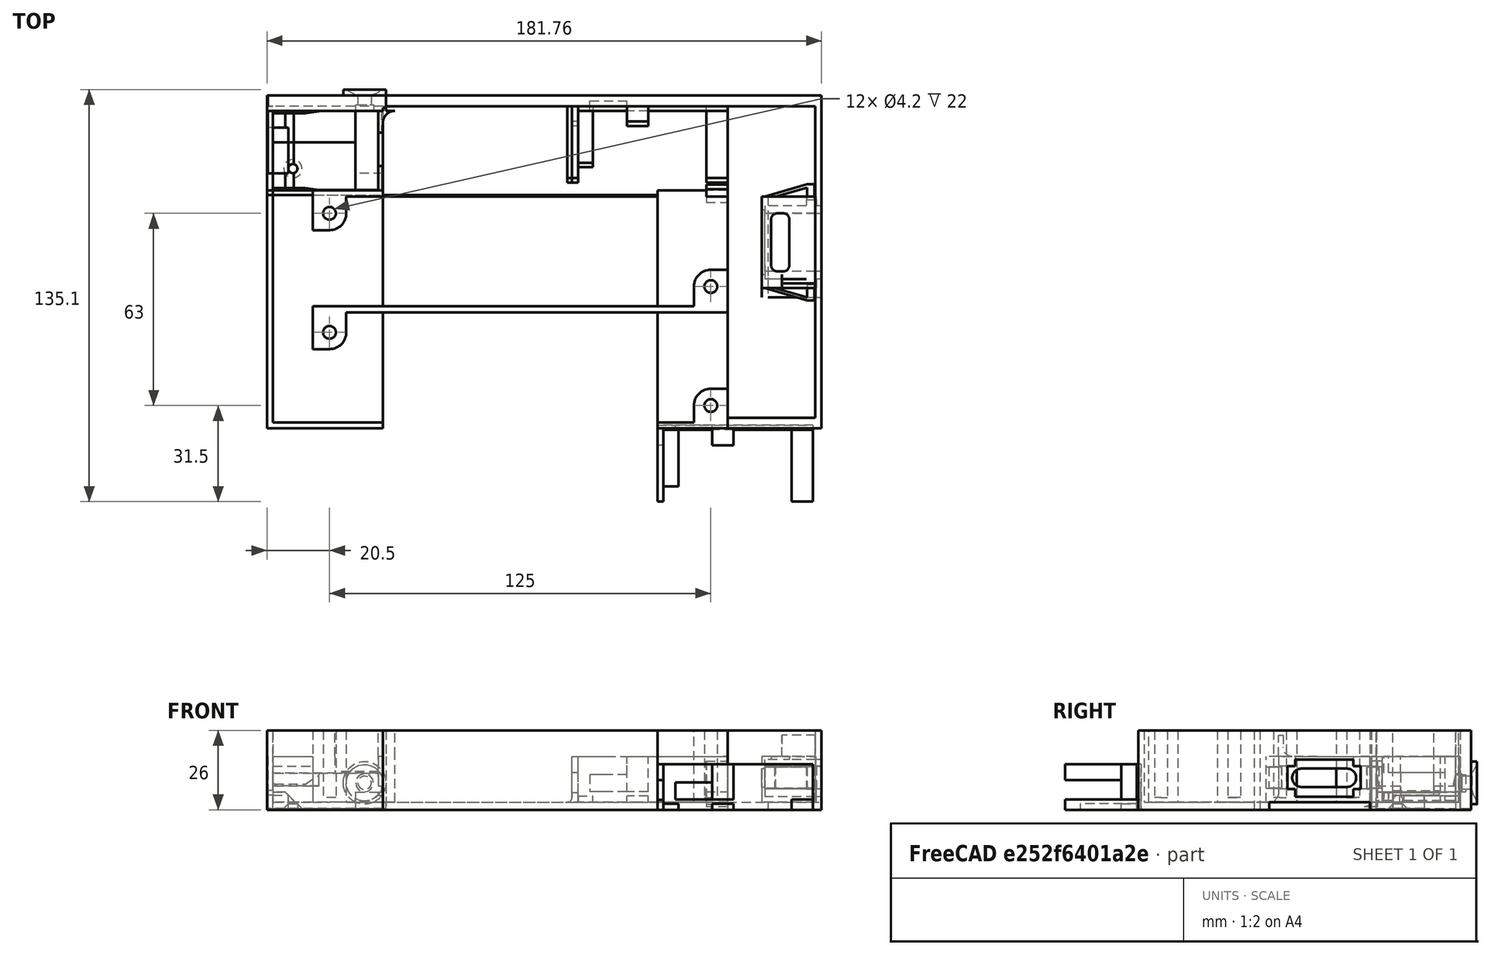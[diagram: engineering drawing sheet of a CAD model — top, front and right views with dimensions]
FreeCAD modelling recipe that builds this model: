
FCSTD DOCUMENT  (FreeCAD 0.21R33771 (Git))
Label: station.lamp.2x42V
License: All rights reserved
LicenseURL: http://en.wikipedia.org/wiki/All_rights_reserved
objects: Part::Extrusion×67, Part::Part2DObjectPython×53, Part::Feature×40, Part::FeaturePython×36, Part::MultiFuse×31, Part::Cut×25, Part::Refine×12, App::DocumentObjectGroup×10, Part::Fuse×5, Part::Box×1
note: 270 computed .brp shape members not serialized (recipe doc carries the construction recipe); baked Part::Feature solids carry a one-line shape summary decoded from their .brp

FEATURE [Part::Box] Box  label="Cube"
  AttacherType = Attacher::AttachEngine3D
  Height = 22
  Length = 11
  Width = 12
FEATURE [Part::Part2DObjectPython] Circle  # Draft 2D object (typed FeaturePython)
  Area = 13.8544
  FirstAngle = 0
  LastAngle = 0
  MakeFace = true
  Placement = pos=(5.5,6.5,22) rot=(0,0,1;0rad)
  Radius = 2.1
FEATURE [Part::Extrusion] Extrusion
  Base = -> Circle
  Dir = (0,0,-8)
  DirMode = 0
  FaceMakerClass = Part::FaceMakerBullseye
  LengthFwd = 0
  LengthRev = 0
  Solid = true
  Symmetric = false
FEATURE [Part::Cut] Cut
  Base = -> Box
  Tool = -> Extrusion
FEATURE [Part::Part2DObjectPython] Rectangle  # Draft 2D object (typed FeaturePython)
  Area = 971.593
  ChamferSize = 0
  Columns = 1
  FilletRadius = 0
  Height = 29.7354
  Length = 32.6747
  MakeFace = true
  Placement = pos=(5.5,6.5,22) rot=(0,0,1;0rad)
  Rows = 1
FEATURE [Part::Part2DObjectPython] Circle001  # Draft 2D object (typed FeaturePython)
  Area = 95.0332
  FirstAngle = 0
  LastAngle = 0
  MakeFace = true
  Placement = pos=(5.5,6.5,22) rot=(0,0,1;0rad)
  Radius = 5.5
FEATURE [Part::Extrusion] Extrusion001
  Base = -> Rectangle
  Dir = (0,0,-32.8426)
  DirMode = 0
  FaceMakerClass = Part::FaceMakerBullseye
  LengthFwd = 0
  LengthRev = 0
  Solid = true
  Symmetric = false
FEATURE [Part::Extrusion] Extrusion002
  Base = -> Circle001
  Dir = (0,0,-44.3564)
  DirMode = 0
  FaceMakerClass = Part::FaceMakerBullseye
  LengthFwd = 0
  LengthRev = 0
  Solid = true
  Symmetric = false
FEATURE [Part::Cut] Cut001
  Base = -> Extrusion001
  Tool = -> Extrusion002
FEATURE [Part::Cut] Cut002
  Base = -> Cut
  Placement = pos=(136,-37,22) rot=(0,1,0;3.14159rad)
  Tool = -> Cut001
FEATURE [Part::FeaturePython] Clone  label="Cut003"  # Draft clone (typed FeaturePython)
  AttacherType = Attacher::AttachEngine3D
  Fuse = false
  Objects = -> [Cut002]
  Placement = pos=(0,1e-15,22) rot=(1,0,0;3.14159rad)
  Scale = (1,1,1)
FEATURE [Part::Part2DObjectPython] Circle002  # Draft 2D object (typed FeaturePython)
  Area = 13.8544
  FirstAngle = 0
  LastAngle = 0
  MakeFace = true
  Placement = pos=(5.5,-6.5,0) rot=(1,0,0;3.14159rad)
  Radius = 2.1
FEATURE [Part::Part2DObjectPython] Circle003  # Draft 2D object (typed FeaturePython)
  Area = 13.8544
  FirstAngle = 0
  LastAngle = 0
  MakeFace = true
  Placement = pos=(130.5,-30.5,3e-15) rot=(1,0,0;3.14159rad)
  Radius = 2.1
FEATURE [Part::Extrusion] Extrusion003
  Base = -> Circle003
  Dir = (0,0,62.0391)
  DirMode = 0
  FaceMakerClass = Part::FaceMakerBullseye
  LengthFwd = 0
  LengthRev = 0
  Solid = true
  Symmetric = false
FEATURE [Part::Extrusion] Extrusion004
  Base = -> Circle002
  Dir = (0,0,161.733)
  DirMode = 0
  FaceMakerClass = Part::FaceMakerBullseye
  LengthFwd = 0
  LengthRev = 0
  Solid = true
  Symmetric = false
FEATURE [Part::Cut] Cut003  label="Cut004"
  Base = -> Cut002
  Tool = -> Extrusion003
FEATURE [Part::Cut] Cut004  label="Cut005"
  Base = -> Clone
  Tool = -> Extrusion004
FEATURE [Part::Part2DObjectPython] Rectangle001  # Draft 2D object (typed FeaturePython)
  Area = 851
  ChamferSize = 0
  Columns = 1
  FilletRadius = 0
  Height = 37
  Length = 23
  MakeFace = true
  Placement = pos=(136,-37,4e-15) rot=(0,1,0;3.14159rad)
  Rows = 1
FEATURE [Part::Part2DObjectPython] Clone2D  label="Rectangle001 (2D)"  # Draft 2D object (typed FeaturePython)
  Fuse = false
  Objects = -> [Rectangle001]
  Placement = pos=(23,-37,4e-15) rot=(0,1,0;3.14159rad)
  Scale = (1,1,1)
FEATURE [Part::Extrusion] Extrusion005
  Base = -> Clone2D
  Dir = (0,0,-4)
  DirMode = 0
  FaceMakerClass = Part::FaceMakerBullseye
  LengthFwd = 0
  LengthRev = 0
  Solid = true
  Symmetric = false
FEATURE [Part::Extrusion] Extrusion006
  Base = -> Rectangle001
  Dir = (0,0,-4)
  DirMode = 0
  FaceMakerClass = Part::FaceMakerBullseye
  LengthFwd = 0
  LengthRev = 0
  Solid = true
  Symmetric = false
FEATURE [Part::Feature] Face
  Placement = pos=(0,1e-15,22) rot=(1,0,0;3.14159rad)
  shape: bbox 11 x 2e-07 x 22 mm, 1 faces, 0 solids (baked)
FEATURE [Part::Extrusion] Extrusion007
  Base = -> Face
  Dir = (0,1,-1e-16)
  DirMode = 0
  FaceMakerClass = Part::FaceMakerBullseye
  LengthFwd = 0
  LengthRev = 0
  Solid = true
  Symmetric = false
FEATURE [Part::Feature] Face001
  shape: bbox 23 x 2e-07 x 4 mm, 1 faces, 0 solids (baked)
FEATURE [Part::Extrusion] Extrusion008
  Base = -> Face001
  Dir = (-6e-16,1,0)
  DirMode = 0
  FaceMakerClass = Part::FaceMakerBullseye
  LengthFwd = 0
  LengthRev = 0
  Solid = true
  Symmetric = false
FEATURE [Part::Feature] Face002
  shape: bbox 23 x 2e-07 x 4 mm, 1 faces, 0 solids (baked)
FEATURE [Part::Extrusion] Extrusion009
  Base = -> Face002
  Dir = (-6e-16,1,0)
  DirMode = 0
  FaceMakerClass = Part::FaceMakerBullseye
  LengthFwd = 0
  LengthRev = 0
  Solid = true
  Symmetric = false
FEATURE [Part::Part2DObjectPython] Rectangle002  # Draft 2D object (typed FeaturePython)
  Area = 3536
  ChamferSize = 0
  Columns = 1
  FilletRadius = 0
  Height = 26
  Length = 136
  MakeFace = true
  Placement = pos=(136,1,-4) rot=(0,0.707107,0.707107;3.14159rad)
  Rows = 1
FEATURE [Part::Extrusion] Extrusion010
  Base = -> Rectangle002
  Dir = (0,2,-4e-16)
  DirMode = 0
  FaceMakerClass = Part::FaceMakerBullseye
  LengthFwd = 0
  LengthRev = 0
  Solid = true
  Symmetric = false
FEATURE [Part::MultiFuse] Fusion
  Placement = pos=(-1.4e-14,40,0) rot=(0,0,1;0rad)
  Shapes = -> [Extrusion005,Cut004,Cut003,Extrusion006]
FEATURE [Part::FeaturePython] Clone001  label="Fusion001"  # Draft clone (typed FeaturePython)
  AttacherType = Attacher::AttachEngine3D
  Fuse = false
  Objects = -> [Fusion]
  Scale = (1,1,1)
FEATURE [Part::MultiFuse] Fusion001  label="Fusion002"
  Shapes = -> [Extrusion007,Extrusion008,Extrusion010,Clone001,Fusion]
FEATURE [Part::MultiFuse] Fusion002  label="Fusion003"
  Shapes = -> [Extrusion009,Fusion001]
FEATURE [Part::Refine] Fusion003  label="Fusion004"
  Source = -> Fusion002
FEATURE [Part::Refine] Slice001_child008  label="Slice001.008"
  Placement = pos=(63.9271,122.311,196.55) rot=(0,0,1;0rad)
FEATURE [Part::Part2DObjectPython] Rectangle003  # Draft 2D object (typed FeaturePython)
  Area = 3532.71
  ChamferSize = 0
  Columns = 1
  FilletRadius = 0
  Height = 62.6067
  Length = 56.4271
  MakeFace = true
  Placement = pos=(151.02,67.5086,-24.944) rot=(1,0,0;1.5708rad)
  Rows = 1
FEATURE [Part::FeaturePython] Slice  # WARN: FeaturePython — macro-defined, semantics opaque (R4)
  Base = -> Slice001_child008
  Mode = 1
  Tolerance = 0
  Tools = -> [Rectangle003]
FEATURE [Part::FeaturePython] Slice_child1  label="Slice.1"  # WARN: FeaturePython — macro-defined, semantics opaque (R4)
  Base = -> Slice
  FilterType = 1
  Invert = false
  OverrideMaxVal = 0
  WindowFrom = 80
  WindowTo = 100
  items = 1
FEATURE [Part::FeaturePython] Slice_child2  label="Slice.2"  # WARN: FeaturePython — macro-defined, semantics opaque (R4)
  Base = -> Slice
  FilterType = 1
  Invert = false
  OverrideMaxVal = 0
  WindowFrom = 80
  WindowTo = 100
  items = 2
FEATURE [Part::Part2DObjectPython] Rectangle004  # Draft 2D object (typed FeaturePython)
  Area = 16535.2
  ChamferSize = 0
  Columns = 1
  FilletRadius = 0
  Height = 229.122
  Length = 72.1676
  MakeFace = true
  Placement = pos=(178.703,-37,-145.137) rot=(0,0.707107,0.707107;3.14159rad)
  Rows = 1
FEATURE [Part::Feature] Face003
  shape: bbox 9.495e-05 x 4.3 x 15 mm, 1 faces, 0 solids (baked)
FEATURE [Part::Extrusion] Extrusion011
  Base = -> Face003
  Dir = (4.5,4.14e-14,-2.35167e-10)
  DirMode = 0
  FaceMakerClass = Part::FaceMakerBullseye
  LengthFwd = 0
  LengthRev = 0
  Placement = pos=(-0.7,1,0) rot=(0,0,1;0rad)
  Solid = true
  Symmetric = false
FEATURE [Part::Part2DObjectPython] Rectangle005  # Draft 2D object (typed FeaturePython)
  Area = 2512.66
  ChamferSize = 0
  Columns = 1
  FilletRadius = 0
  Height = 57.2002
  Length = 43.9275
  MakeFace = true
  Placement = pos=(113.7,-22.7052,-12.794) rot=(0.57735,-0.57735,-0.57735;2.0944rad)
  Rows = 1
FEATURE [Part::Part2DObjectPython] Rectangle006  # Draft 2D object (typed FeaturePython)
  Area = 65540.4
  ChamferSize = 0
  Columns = 1
  FilletRadius = 0
  Height = 220.903
  Length = 296.693
  MakeFace = true
  Placement = pos=(-69.999,-3.62e-14,-154.145) rot=(1,0,0;1.5708rad)
  Rows = 1
FEATURE [Part::FeaturePython] Slice003  # WARN: FeaturePython — macro-defined, semantics opaque (R4)
  Base = -> Fusion003
  Mode = 1
  Tolerance = 0
  Tools = -> [Rectangle006]
FEATURE [App::DocumentObjectGroup] GrExplode_Slice003  label="Exploded Slice003"
FEATURE [Part::FeaturePython] Slice003_child0  label="Slice003.0"  # WARN: FeaturePython — macro-defined, semantics opaque (R4)
  Base = -> Slice003
  FilterType = 1
  Invert = false
  OverrideMaxVal = 0
  WindowFrom = 80
  WindowTo = 100
  items = 0
FEATURE [Part::FeaturePython] Slice003_child1  label="Slice003.1"  # WARN: FeaturePython — macro-defined, semantics opaque (R4)
  Base = -> Slice003
  FilterType = 1
  Invert = false
  OverrideMaxVal = 0
  Placement = pos=(0,1,0) rot=(0,0,1;0rad)
  WindowFrom = 80
  WindowTo = 100
  items = 1
FEATURE [Part::FeaturePython] Slice003_child2  label="Slice003.2"  # WARN: FeaturePython — macro-defined, semantics opaque (R4)
  Base = -> Slice003
  FilterType = 1
  Invert = false
  OverrideMaxVal = 0
  Placement = pos=(0,1,0) rot=(0,0,1;0rad)
  WindowFrom = 80
  WindowTo = 100
  items = 2
FEATURE [Part::Part2DObjectPython] Line009  # Draft 2D object (typed FeaturePython)
  Area = 0
  ChamferSize = 0
  Closed = false
  End = (23,-17.5,-1.5)
  FilletRadius = 0
  Length = 1.5
  MakeFace = true
  Placement = pos=(23,-17.5,4e-15) rot=(0.57735,0.57735,0.57735;2.0944rad)
  Points = (2) [(0,0,0),(0,-1.5,-2.66454e-15)]
  Start = (23,-17.5,3.6e-15)
  Subdivisions = 0
FEATURE [Part::Feature] Face004
  shape: bbox 23 x 37 x 9.495e-05 mm, 1 faces, 0 solids (baked)
FEATURE [Part::Extrusion] Extrusion012
  Base = -> Face004
  Dir = (0,0,-1.5)
  DirMode = 0
  FaceMakerClass = Part::FaceMakerBullseye
  LengthFwd = 0
  LengthRev = 0
  Solid = true
  Symmetric = false
FEATURE [Part::Feature] Face005
  Placement = pos=(-1.4e-14,40,0) rot=(0,0,1;0rad)
  shape: bbox 23 x 37 x 9.495e-05 mm, 1 faces, 0 solids (baked)
FEATURE [Part::Extrusion] Extrusion013
  Base = -> Face005
  Dir = (0,0,-1.5)
  DirMode = 0
  FaceMakerClass = Part::FaceMakerBullseye
  LengthFwd = 0
  LengthRev = 0
  Solid = true
  Symmetric = false
FEATURE [Part::Feature] Face006
  Placement = pos=(-1.4e-14,40,0) rot=(0,0,1;0rad)
  shape: bbox 23 x 37 x 9.495e-05 mm, 1 faces, 0 solids (baked)
FEATURE [Part::Extrusion] Extrusion014
  Base = -> Face006
  Dir = (0,0,-1.5)
  DirMode = 0
  FaceMakerClass = Part::FaceMakerBullseye
  LengthFwd = 0
  LengthRev = 0
  Solid = true
  Symmetric = false
FEATURE [Part::Feature] Face007
  shape: bbox 23 x 37 x 2.037e-05 mm, 1 faces, 0 solids (baked)
FEATURE [Part::Extrusion] Extrusion015
  Base = -> Face007
  Dir = (0,0,-1.5)
  DirMode = 0
  FaceMakerClass = Part::FaceMakerBullseye
  LengthFwd = 0
  LengthRev = 0
  Solid = true
  Symmetric = false
FEATURE [Part::Part2DObjectPython] Rectangle007  # Draft 2D object (typed FeaturePython)
  Area = 5888.28
  ChamferSize = 0
  Columns = 1
  FilletRadius = 0
  Height = 60.4657
  Length = 97.3822
  MakeFace = true
  Placement = pos=(94.0945,-36,-42.8831) rot=(1,0,0;1.5708rad)
  Rows = 1
FEATURE [Part::FeaturePython] Slice_child0  label="Slice.0"  # WARN: FeaturePython — macro-defined, semantics opaque (R4)
  Base = -> Slice
  FilterType = 1
  Invert = false
  OverrideMaxVal = 0
  Placement = pos=(81.7528,194.877,-8.54915) rot=(0,0,-1;1.5708rad)
  WindowFrom = 80
  WindowTo = 100
  items = 0
FEATURE [Part::MultiFuse] Fusion004  label="Fusion005"
  Placement = pos=(93.9914,120.377,-12.5492) rot=(0,0,-1;1.5708rad)
  Shapes = -> [Slice_child1,Slice_child2]
FEATURE [App::DocumentObjectGroup] GrExplode_Slice  label="Exploded Slice"
  Group = -> [Fusion004]
FEATURE [Part::FeaturePython] Slice001  # WARN: FeaturePython — macro-defined, semantics opaque (R4)
  Base = -> Fusion004
  Mode = 1
  Tolerance = 0
  Tools = -> [Rectangle004]
FEATURE [Part::FeaturePython] Slice001_child1  label="Slice001.1"  # WARN: FeaturePython — macro-defined, semantics opaque (R4)
  Base = -> Slice001
  FilterType = 1
  Invert = false
  OverrideMaxVal = 0
  Placement = pos=(3.2,1,1.5) rot=(0,0,1;0rad)
  WindowFrom = 80
  WindowTo = 100
  items = 1
FEATURE [Part::FeaturePython] Slice001_child2  label="Slice001.2"  # WARN: FeaturePython — macro-defined, semantics opaque (R4)
  Base = -> Slice001
  FilterType = 1
  Invert = false
  OverrideMaxVal = 0
  Placement = pos=(-0.7,1,0) rot=(0,0,1;0rad)
  WindowFrom = 80
  WindowTo = 100
  items = 2
FEATURE [Part::FeaturePython] Slice002  # WARN: FeaturePython — macro-defined, semantics opaque (R4)
  Base = -> Slice001_child1
  Mode = 1
  Tolerance = 0
  Tools = -> [Rectangle005]
FEATURE [Part::FeaturePython] Slice002_child0  label="Slice002.0"  # WARN: FeaturePython — macro-defined, semantics opaque (R4)
  Base = -> Slice002
  FilterType = 1
  Invert = false
  OverrideMaxVal = 0
  Placement = pos=(-0.7,0,0) rot=(0,0,1;0rad)
  WindowFrom = 80
  WindowTo = 100
  items = 0
FEATURE [App::DocumentObjectGroup] GrExplode_Slice002  label="Exploded Slice002"
  Group = -> [Slice002_child0]
FEATURE [Part::MultiFuse] Fusion005  label="Fusion006"
  Shapes = -> [Slice003_child1,Slice003_child0,Slice003_child2,Slice001_child1,Slice001_child2,Extrusion011]
FEATURE [App::DocumentObjectGroup] GrExplode_Slice001  label="Exploded Slice001"
  Group = -> [Fusion005]
FEATURE [Part::Refine] Fusion006  label="Fusion007"
  Source = -> Fusion005
FEATURE [Part::Cut] Cut005  label="Cut006"
  Base = -> Fusion006
  Tool = -> Extrusion015
FEATURE [Part::Cut] Cut006  label="Cut007"
  Base = -> Cut005
  Tool = -> Extrusion014
FEATURE [Part::Cut] Cut007  label="Cut008"
  Base = -> Cut006
  Tool = -> Extrusion013
FEATURE [Part::Cut] Cut008  label="Cut009"
  Base = -> Cut007
  Tool = -> Extrusion012
FEATURE [Part::FeaturePython] Slice004  # WARN: FeaturePython — macro-defined, semantics opaque (R4)
  Base = -> Cut008
  Mode = 1
  Tolerance = 0
  Tools = -> [Rectangle007]
FEATURE [Part::FeaturePython] Slice004_child0  label="Slice004.0"  # WARN: FeaturePython — macro-defined, semantics opaque (R4)
  Base = -> Slice004
  FilterType = 1
  Invert = false
  OverrideMaxVal = 0
  WindowFrom = 80
  WindowTo = 100
  items = 0
FEATURE [Part::FeaturePython] Slice004_child1  label="Slice004.1"  # WARN: FeaturePython — macro-defined, semantics opaque (R4)
  Base = -> Slice004
  FilterType = 1
  Invert = false
  OverrideMaxVal = 0
  WindowFrom = 80
  WindowTo = 100
  items = 1
FEATURE [Part::FeaturePython] Slice004_child2  label="Slice004.2"  # WARN: FeaturePython — macro-defined, semantics opaque (R4)
  Base = -> Slice004
  FilterType = 1
  Invert = false
  OverrideMaxVal = 0
  WindowFrom = 80
  WindowTo = 100
  items = 2
FEATURE [Part::Part2DObjectPython] Line010  # Draft 2D object (typed FeaturePython)
  Area = 0
  ChamferSize = 0
  Closed = false
  End = (11,39,11)
  FilletRadius = 0
  Length = 1
  MakeFace = true
  Placement = pos=(11,40,11) rot=(0.57735,0.57735,0.57735;2.0944rad)
  Points = (2) [(0,0,0),(-1,0,0)]
  Start = (11,40,11)
  Subdivisions = 0
FEATURE [Part::Part2DObjectPython] Rectangle008  # Draft 2D object (typed FeaturePython)
  Area = 23.5
  ChamferSize = 0
  Columns = 1
  FilletRadius = 0
  Height = 23.5
  Length = 1
  MakeFace = true
  Placement = pos=(11,39,-1.5) rot=(0.57735,0.57735,0.57735;2.0944rad)
  Rows = 1
FEATURE [Part::Extrusion] Extrusion016
  Base = -> Rectangle008
  Dir = (12,0,0)
  DirMode = 0
  FaceMakerClass = Part::FaceMakerBullseye
  LengthFwd = 0
  LengthRev = 0
  Solid = true
  Symmetric = false
FEATURE [Part::MultiFuse] Fusion007  label="Fusion008"
  Placement = pos=(-28.7,104.6,2.5) rot=(0,0,1;0rad)
  Shapes = -> [Slice004_child1,Slice004_child2]
FEATURE [Part::Part2DObjectPython] Line012  # Draft 2D object (typed FeaturePython)
  Area = 0
  ChamferSize = 0
  Closed = false
  End = (125,-35,11)
  FilletRadius = 0
  Length = 1
  MakeFace = true
  Placement = pos=(125,-36,11) rot=(0.57735,-0.57735,-0.57735;2.0944rad)
  Points = (2) [(0,0,0),(-1,0,0)]
  Start = (125,-36,11)
  Subdivisions = 0
FEATURE [Part::Part2DObjectPython] Rectangle009  # Draft 2D object (typed FeaturePython)
  Area = 23.5
  ChamferSize = 0
  Columns = 1
  FilletRadius = 0
  Height = 23.5
  Length = 1
  MakeFace = true
  Placement = pos=(125,-35,-1.5) rot=(0.57735,-0.57735,-0.57735;2.0944rad)
  Rows = 1
FEATURE [Part::Extrusion] Extrusion017
  Base = -> Rectangle009
  Dir = (-12,0,0)
  DirMode = 0
  FaceMakerClass = Part::FaceMakerBullseye
  LengthFwd = 0
  LengthRev = 0
  Solid = true
  Symmetric = false
FEATURE [Part::Feature] Face008
  Placement = pos=(113,-35,-1.5) rot=(0.57735,-0.57735,-0.57735;2.0944rad)
  shape: bbox 9.505e-05 x 1 x 23.5 mm, 1 faces, 0 solids (baked)
FEATURE [Part::Part2DObjectPython] Rectangle010  # Draft 2D object (typed FeaturePython)
  Area = 540.5
  ChamferSize = 0
  Columns = 1
  FilletRadius = 0
  Height = 23.5
  Length = 23
  MakeFace = true
  Placement = pos=(1.4e-14,-36,-1.5) rot=(1,0,0;1.5708rad)
  Rows = 1
FEATURE [Part::Extrusion] Extrusion019
  Base = -> Rectangle010
  Dir = (-6e-16,1,-2e-16)
  DirMode = 0
  FaceMakerClass = Part::FaceMakerBullseye
  LengthFwd = 0
  LengthRev = 0
  Solid = true
  Symmetric = false
FEATURE [Part::Feature] Face009
  Placement = pos=(23,39,-1.5) rot=(0.57735,0.57735,0.57735;2.0944rad)
  shape: bbox 9.505e-05 x 1 x 23.5 mm, 1 faces, 0 solids (baked)
FEATURE [Part::Part2DObjectPython] Rectangle011  # Draft 2D object (typed FeaturePython)
  Area = 540.5
  ChamferSize = 0
  Columns = 1
  FilletRadius = 0
  Height = 23.5
  Length = 23
  MakeFace = true
  Placement = pos=(136,40,-1.5) rot=(0,0.707107,0.707107;3.14159rad)
  Rows = 1
FEATURE [Part::Extrusion] Extrusion021
  Base = -> Rectangle011
  Dir = (0,-1,2e-16)
  DirMode = 0
  FaceMakerClass = Part::FaceMakerBullseye
  LengthFwd = 0
  LengthRev = 0
  Solid = true
  Symmetric = false
FEATURE [Part::MultiFuse] Fusion008  label="Fusion009"
  Shapes = -> [Extrusion017,Extrusion019,Extrusion016,Extrusion021,Slice004_child0]
FEATURE [Part::Refine] Fusion009  label="Fusion010"
  Source = -> Fusion008
FEATURE [Part::Part2DObjectPython] Line014  # Draft 2D object (typed FeaturePython)
  Area = 0
  ChamferSize = 0
  Closed = false
  End = (1.47e-14,-37,22)
  FilletRadius = 0
  Length = 1
  MakeFace = true
  Placement = pos=(1.4e-14,-36,22) rot=(0.57735,-0.57735,-0.57735;2.0944rad)
  Points = (2) [(0,0,0),(1,0,-1.69085e-16)]
  Start = (1.42e-14,-36,22)
  Subdivisions = 0
FEATURE [Part::Feature] Face010
  shape: bbox 23 x 9.505e-05 x 26 mm, 1 faces, 0 solids (baked)
FEATURE [Part::Extrusion] Extrusion022
  Base = -> Face010
  Dir = (6e-16,-1,2e-15)
  DirMode = 0
  FaceMakerClass = Part::FaceMakerBullseye
  LengthFwd = 0
  LengthRev = 0
  Solid = true
  Symmetric = false
FEATURE [Part::Feature] Face011
  shape: bbox 23 x 9.505e-05 x 26 mm, 1 faces, 0 solids (baked)
FEATURE [Part::Extrusion] Extrusion023
  Base = -> Face011
  Dir = (2e-16,-1,5e-16)
  DirMode = 0
  FaceMakerClass = Part::FaceMakerBullseye
  LengthFwd = 0
  LengthRev = 0
  Solid = true
  Symmetric = false
FEATURE [Part::Part2DObjectPython] Line015  # Draft 2D object (typed FeaturePython)
  Area = 0
  ChamferSize = 0
  Closed = false
  End = (23,41,22)
  FilletRadius = 0
  Length = 1
  MakeFace = true
  Placement = pos=(23,40,22) rot=(0,0,1;1.5708rad)
  Points = (2) [(0,0,0),(1,0,0)]
  Start = (23,40,22)
  Subdivisions = 0
FEATURE [Part::Feature] Face012
  shape: bbox 23 x 9.495e-05 x 26 mm, 1 faces, 0 solids (baked)
FEATURE [Part::Extrusion] Extrusion024
  Base = -> Face012
  Dir = (-2e-16,1,2e-16)
  DirMode = 0
  FaceMakerClass = Part::FaceMakerBullseye
  LengthFwd = 0
  LengthRev = 0
  Solid = true
  Symmetric = false
FEATURE [Part::Feature] Face013
  shape: bbox 23 x 9.505e-05 x 26 mm, 1 faces, 0 solids (baked)
FEATURE [Part::Extrusion] Extrusion025
  Base = -> Face013
  Dir = (-2e-16,1,1.6e-15)
  DirMode = 0
  FaceMakerClass = Part::FaceMakerBullseye
  LengthFwd = 0
  LengthRev = 0
  Solid = true
  Symmetric = false
FEATURE [Part::MultiFuse] Fusion010  label="Fusion011"
  Shapes = -> [Extrusion023,Extrusion022,Extrusion024,Extrusion025,Fusion009]
FEATURE [Part::Refine] Fusion011  label="Fusion012"
  Source = -> Fusion010
FEATURE [Part::MultiFuse] Fusion005002002014004003003002009002010004002003006003008008004007002004008002005011019002002002012002
FEATURE [Part::Part2DObjectPython] Rectangle012  # Draft 2D object (typed FeaturePython)
  ChamferSize = 0
  Columns = 1
  FilletRadius = 0
  Height = 74.0625
  Length = 50.4262
  MakeFace = true
  Placement = pos=(152.909,-168.503,-194.387) rot=(1,0,0;1.5708rad)
  Rows = 1
FEATURE [Part::Part2DObjectPython] Rectangle013  # Draft 2D object (typed FeaturePython)
  Area = 24058.8
  ChamferSize = 0
  Columns = 1
  FilletRadius = 0
  Height = 153.205
  Length = 157.037
  MakeFace = true
  Placement = pos=(77.9842,-28.2917,-189.501) rot=(0,0,-1;1.5708rad)
  Rows = 1
FEATURE [Part::FeaturePython] Slice005  # WARN: FeaturePython — macro-defined, semantics opaque (R4)
  Base = -> Fusion005002002014004003003002009002010004002003006003008008004007002004008002005011019002002002012002
  Mode = 1
  Tolerance = 0
  Tools = -> [Rectangle012]
FEATURE [Part::FeaturePython] Slice_child003  label="Slice.003"  # WARN: FeaturePython — macro-defined, semantics opaque (R4)
  Base = -> Slice005
  FilterType = 1
  Invert = false
  OverrideMaxVal = 0
  WindowFrom = 80
  WindowTo = 100
  items = 0
FEATURE [Part::FeaturePython] Slice006  # WARN: FeaturePython — macro-defined, semantics opaque (R4)
  Base = -> Slice_child003
  Mode = 1
  Tolerance = 0
  Tools = -> [Rectangle013]
FEATURE [Part::FeaturePython] Slice001_child009  label="Slice001.009"  # WARN: FeaturePython — macro-defined, semantics opaque (R4)
  Base = -> Slice006
  FilterType = 1
  Invert = false
  OverrideMaxVal = 0
  Placement = pos=(-34.5709,-121.99,188.001) rot=(0,0,1;0rad)
  WindowFrom = 80
  WindowTo = 100
  items = 1
FEATURE [Part::Refine] Slice001_child010  label="Slice001.010"
  Placement = pos=(127.549,-38.5,-261.892) rot=(0,-0.707107,0.707107;3.14159rad)
  Source = -> Slice001_child009
FEATURE [Part::Part2DObjectPython] Line019  # Draft 2D object (typed FeaturePython)
  Area = 0
  ChamferSize = 0
  Closed = false
  End = (23,-37,-1)
  FilletRadius = 0
  Length = 3
  MakeFace = true
  Placement = pos=(23,-40,-1) rot=(0.57735,0.57735,0.57735;2.0944rad)
  Points = (2) [(0,0,0),(3,2.49441e-09,-1.58593e-11)]
  Start = (23,-40,-1)
  Subdivisions = 0
FEATURE [Part::Part2DObjectPython] Rectangle014  # Draft 2D object (typed FeaturePython)
  Area = 12480.5
  ChamferSize = 0
  Columns = 1
  FilletRadius = 0
  Height = 104.133
  Length = 119.851
  MakeFace = true
  Placement = pos=(65.3633,29.745,-4) rot=(0.707107,-0.707107,0;3.14159rad)
  Rows = 1
FEATURE [Part::FeaturePython] Slice007  # WARN: FeaturePython — macro-defined, semantics opaque (R4)
  Base = -> Slice001_child010
  Mode = 1
  Tolerance = 0
  Tools = -> [Rectangle014]
FEATURE [App::DocumentObjectGroup] GrExplode_Slice007  label="Exploded Slice007"
FEATURE [Part::FeaturePython] Slice007_child0  label="Slice007.0"  # WARN: FeaturePython — macro-defined, semantics opaque (R4)
  Base = -> Slice007
  FilterType = 1
  Invert = false
  OverrideMaxVal = 0
  WindowFrom = 80
  WindowTo = 100
  items = 0
FEATURE [Part::Feature] Face014
  shape: bbox 0.0001337 x 5 x 1.65 mm, 1 faces, 0 solids (baked)
FEATURE [Part::Extrusion] Extrusion026
  Base = -> Face014
  Dir = (14.1794,4.79232e-08,2.885e-13)
  DirMode = 0
  FaceMakerClass = Part::FaceMakerBullseye
  LengthFwd = 0
  LengthRev = 0
  Solid = true
  Symmetric = false
FEATURE [Part::MultiFuse] Fusion005002002014004003003002009002010004002003006003008008004007002004008002005011019002002002012003
  Placement = pos=(-1.12479e-11,6.4929e-09,-1.6) rot=(0,0,1;0rad)
  Shapes = -> [Slice007_child0,Extrusion026]
FEATURE [Part::Part2DObjectPython] Rectangle015  # Draft 2D object (typed FeaturePython)
  Area = 189.759
  ChamferSize = 0
  Columns = 1
  FilletRadius = 0
  Height = 34.5
  Length = 5.50025
  MakeFace = true
  Placement = pos=(21.5,-52,-3.95) rot=(0,0,1;1.5708rad)
  Rows = 1
FEATURE [Part::Extrusion] Extrusion027
  Base = -> Rectangle015
  Dir = (2.2392e-09,1.32254e-08,7.85)
  DirMode = 0
  FaceMakerClass = Part::FaceMakerBullseye
  LengthFwd = 0
  LengthRev = 0
  Placement = pos=(4e-15,-1.24722e-10,-0.15) rot=(0,0,1;0rad)
  Solid = true
  Symmetric = false
FEATURE [Part::Cut] Cut009  label="Cut010"
  Base = -> Fusion005002002014004003003002009002010004002003006003008008004007002004008002005011019002002002012003
  Placement = pos=(-6.04654e-08,45.1,-38.5) rot=(-1,0,0;1.5708rad)
  Tool = -> Extrusion027
FEATURE [Part::Part2DObjectPython] Rectangle016  # Draft 2D object (typed FeaturePython)
  Area = 3801.6
  ChamferSize = 0
  Columns = 1
  FilletRadius = 0
  Height = 36
  Length = 105.6
  MakeFace = true
  Placement = pos=(23,68.6,-4) rot=(0.707107,-0.707107,0;3.14159rad)
  Rows = 1
FEATURE [Part::Extrusion] Extrusion028
  Base = -> Rectangle016
  Dir = (-4.02896e-11,9.80014e-11,2.5)
  DirMode = 0
  FaceMakerClass = Part::FaceMakerBullseye
  LengthFwd = 0
  LengthRev = 0
  Solid = true
  Symmetric = false
FEATURE [Part::Part2DObjectPython] Circle004  # Draft 2D object (typed FeaturePython)
  Area = 7.06956
  FirstAngle = 0
  LastAngle = 0
  MakeFace = true
  Placement = pos=(-6.48965,49.6501,-1.00025) rot=(1,0,0;3.14159rad)
  Radius = 1.5001
FEATURE [Part::Extrusion] Extrusion029
  Base = -> Circle004
  Dir = (-6.49882e-09,-1.24878e-09,-29.8695)
  DirMode = 0
  FaceMakerClass = Part::FaceMakerBullseye
  LengthFwd = 0
  LengthRev = 0
  Solid = true
  Symmetric = false
FEATURE [Part::Cut] Cut010  label="Cut011"
  Base = -> Extrusion028
  Tool = -> Extrusion029
FEATURE [Part::Part2DObjectPython] Rectangle017  # Draft 2D object (typed FeaturePython)
  Area = 2745.6
  ChamferSize = 0
  Columns = 1
  FilletRadius = 0
  Height = 26
  Length = 105.6
  MakeFace = true
  Placement = pos=(-13,68.6,-4) rot=(0.57735,-0.57735,-0.57735;2.0944rad)
  Rows = 1
FEATURE [Part::Part2DObjectPython] Rectangle018  # Draft 2D object (typed FeaturePython)
  Area = 47
  ChamferSize = 0
  Columns = 1
  FilletRadius = 0
  Height = 23.5
  Length = 2
  MakeFace = true
  Placement = pos=(1.3e-14,-35,-1.5) rot=(0.57735,-0.57735,-0.57735;2.0944rad)
  Rows = 1
FEATURE [Part::Extrusion] Extrusion030
  Base = -> Rectangle018
  Dir = (-13,-2.9e-15,1.4e-15)
  DirMode = 0
  FaceMakerClass = Part::FaceMakerBullseye
  LengthFwd = 0
  LengthRev = 0
  Solid = true
  Symmetric = false
FEATURE [Part::Part2DObjectPython] Line026  # Draft 2D object (typed FeaturePython)
  Area = 0
  ChamferSize = 0
  Closed = false
  End = (-15,-37,22)
  FilletRadius = 0
  Length = 2
  MakeFace = true
  Placement = pos=(-13,-37,22) rot=(0,0,1;0rad)
  Points = (2) [(0,0,0),(-2,0,0)]
  Start = (-13,-37,22)
  Subdivisions = 0
FEATURE [Part::Extrusion] Extrusion031
  Base = -> Rectangle017
  Dir = (-2,4e-16,-3.2232e-11)
  DirMode = 0
  FaceMakerClass = Part::FaceMakerBullseye
  LengthFwd = 0
  LengthRev = 0
  Solid = true
  Symmetric = false
FEATURE [Part::MultiFuse] Fusion005002002014004003003002009002010004002003006003008008004007002004008002005011019002002002012004
  Shapes = -> [Extrusion031,Extrusion030]
FEATURE [Part::MultiFuse] Fusion005002002014004003003002009002010004002003006003008008004007002004008002005011019002002002012005
  Shapes = -> [Fusion005002002014004003003002009002010004002003006003008008004007002004008002005011019002002002012004,Cut010]
FEATURE [Part::Part2DObjectPython] Rectangle019  # Draft 2D object (typed FeaturePython)
  Area = 69
  ChamferSize = 0
  Columns = 1
  FilletRadius = 0
  Height = 2.5
  Length = 27.6
  MakeFace = true
  Placement = pos=(23,41,-4) rot=(0.57735,0.57735,0.57735;2.0944rad)
  Rows = 1
FEATURE [Part::Extrusion] Extrusion032
  Base = -> Rectangle019
  Dir = (113,5.02e-14,1.82115e-09)
  DirMode = 0
  FaceMakerClass = Part::FaceMakerBullseye
  LengthFwd = 0
  LengthRev = 0
  Placement = pos=(2.6823e-11,-1.5,9.6466e-10) rot=(0,0,1;0rad)
  Solid = true
  Symmetric = false
FEATURE [Part::Part2DObjectPython] Line028  # Draft 2D object (typed FeaturePython)
  Area = 0
  ChamferSize = 0
  Closed = false
  End = (136,43.2,-1.5)
  FilletRadius = 0
  Length = 0.6
  MakeFace = true
  Placement = pos=(135.4,43.2,-1.5) rot=(0,0,1;3.14159rad)
  Points = (2) [(0,0,0),(-0.6,0,1.55798e-10)]
  Start = (135.4,43.2,-1.5)
  Subdivisions = 0
FEATURE [Part::Part2DObjectPython] Rectangle020  # Draft 2D object (typed FeaturePython)
  Area = 5716.63
  ChamferSize = 0
  Columns = 1
  FilletRadius = 0
  Height = 112.818
  Length = 50.6711
  MakeFace = true
  Placement = pos=(30.41,41,-71.6025) rot=(0,0.707107,0.707107;3.14159rad)
  Rows = 1
FEATURE [Part::FeaturePython] Slice008  # WARN: FeaturePython — macro-defined, semantics opaque (R4)
  Base = -> Fusion005002002014004003003002009002010004002003006003008008004007002004008002005011019002002002012005
  Mode = 1
  Tolerance = 0
  Tools = -> [Rectangle020]
FEATURE [Part::FeaturePython] Slice008_child0  label="Slice008.0"  # WARN: FeaturePython — macro-defined, semantics opaque (R4)
  Base = -> Slice008
  FilterType = 1
  Invert = false
  OverrideMaxVal = 0
  Placement = pos=(2.6819e-11,-1.5,9.64661e-10) rot=(0,0,1;0rad)
  WindowFrom = 80
  WindowTo = 100
  items = 0
FEATURE [App::DocumentObjectGroup] GrExplode_Slice008  label="Exploded Slice008"
  Group = -> [Slice008_child0]
FEATURE [Part::FeaturePython] Slice008_child1  label="Slice008.1"  # WARN: FeaturePython — macro-defined, semantics opaque (R4)
  Base = -> Slice008
  FilterType = 1
  Invert = false
  OverrideMaxVal = 0
  WindowFrom = 80
  WindowTo = 100
  items = 1
FEATURE [Part::Part2DObjectPython] Rectangle021  # Draft 2D object (typed FeaturePython)
  Area = 540.5
  ChamferSize = 0
  Columns = 1
  FilletRadius = 0
  Height = 23.5
  Length = 23
  MakeFace = true
  Placement = pos=(136,41,-1.5) rot=(0,0.707107,0.707107;3.14159rad)
  Rows = 1
FEATURE [Part::Extrusion] Extrusion033
  Base = -> Rectangle021
  Dir = (0,-12.9512,-2.3e-14)
  DirMode = 0
  FaceMakerClass = Part::FaceMakerBullseye
  LengthFwd = 0
  LengthRev = 0
  Solid = true
  Symmetric = false
FEATURE [Part::Cut] Cut011  label="Cut012"
  Base = -> Fusion011
  Tool = -> Extrusion033
FEATURE [Part::Feature] Face016
  Placement = pos=(-24.9,105.6,2.5) rot=(0,0,1;0rad)
  shape: bbox 9.496e-05 x 4.3 x 15 mm, 1 faces, 0 solids (baked)
FEATURE [Part::Extrusion] Extrusion034
  Base = -> Face016
  Dir = (-0.6,-5.5e-15,3.13556e-11)
  DirMode = 0
  FaceMakerClass = Part::FaceMakerBullseye
  LengthFwd = 0
  LengthRev = 0
  Solid = true
  Symmetric = false
FEATURE [Part::Cut] Cut012  label="Cut013"
  Base = -> Fusion007
  Tool = -> Extrusion034
FEATURE [Part::Feature] Face017
  Placement = pos=(34.5271,227.911,199.05) rot=(0,0,1;0rad)
  shape: bbox 9.496e-05 x 4.3 x 15 mm, 1 faces, 0 solids (baked)
FEATURE [Part::Extrusion] Extrusion035
  Base = -> Face017
  Dir = (3.9,3.63e-14,-2.03811e-10)
  DirMode = 0
  FaceMakerClass = Part::FaceMakerBullseye
  LengthFwd = 0
  LengthRev = 0
  Solid = true
  Symmetric = false
FEATURE [Part::Cut] Cut013  label="Cut014"
  Base = -> Cut012
  Tool = -> Extrusion035
FEATURE [Part::Feature] Face018
  shape: bbox 7 x 9.496e-05 x 15 mm, 1 faces, 0 solids (baked)
FEATURE [Part::Extrusion] Extrusion036
  Base = -> Face018
  Dir = (3.19e-14,-2.4,3.08781e-10)
  DirMode = 0
  FaceMakerClass = Part::FaceMakerBullseye
  LengthFwd = 0
  LengthRev = 0
  Solid = true
  Symmetric = false
FEATURE [Part::MultiFuse] Fusion005002002014004003003002009002010004002003006003008008004007002004008002005011019002002002012006
  Shapes = -> [Extrusion036,Cut013]
FEATURE [App::DocumentObjectGroup] GrExplode_Slice004  label="Exploded Slice004"
  Group = -> [Fusion008,Fusion005002002014004003003002009002010004002003006003008008004007002004008002005011019002002002012006]
FEATURE [Part::Feature] Face019
  Placement = pos=(2.6823e-11,-1.5,9.6466e-10) rot=(0,0,1;0rad)
  shape: bbox 113 x 2.001e-07 x 2.5 mm, 1 faces, 0 solids (baked)
FEATURE [Part::Extrusion] Extrusion037
  Base = -> Face019
  Dir = (-7e-16,1.5,-5.88008e-11)
  DirMode = 0
  FaceMakerClass = Part::FaceMakerBullseye
  LengthFwd = 0
  LengthRev = 0
  Solid = true
  Symmetric = false
FEATURE [Part::MultiFuse] Fusion005002002014004003003002009002010004002003006003008008004007002004008002005011019002002002012007
  Shapes = -> [Extrusion037,Extrusion032]
FEATURE [Part::Feature] Face020
  Placement = pos=(2.6819e-11,-1.5,9.64661e-10) rot=(0,0,1;0rad)
  shape: bbox 36 x 2.865e-07 x 2.5 mm, 1 faces, 0 solids (baked)
FEATURE [Part::Extrusion] Extrusion038
  Base = -> Face020
  Dir = (-3e-16,1.5,-5.88008e-11)
  DirMode = 0
  FaceMakerClass = Part::FaceMakerBullseye
  LengthFwd = 0
  LengthRev = 0
  Solid = true
  Symmetric = false
FEATURE [Part::Feature] Face021
  Placement = pos=(2.6819e-11,-1.5,9.64661e-10) rot=(0,0,1;0rad)
  shape: bbox 2 x 2.708e-07 x 26 mm, 1 faces, 0 solids (baked)
FEATURE [Part::Extrusion] Extrusion039
  Base = -> Face021
  Dir = (3e-16,1.5,-5.88006e-11)
  DirMode = 0
  FaceMakerClass = Part::FaceMakerBullseye
  LengthFwd = 0
  LengthRev = 0
  Solid = true
  Symmetric = false
FEATURE [Part::MultiFuse] Fusion005002002014004003003002009002010004002003006003008008004007002004008002005011019002002002012008
  Shapes = -> [Extrusion039,Extrusion038,Fusion005002002014004003003002009002010004002003006003008008004007002004008002005011019002002002012007]
FEATURE [Part::Refine] Slice003_child002  label="Slice003.002"
  Placement = pos=(123.12,-132.503,213.501) rot=(0,0,1;3.14159rad)
  Source = -> Slice003_child1
FEATURE [Part::Part2DObjectPython] Rectangle023  # Draft 2D object (typed FeaturePython)
  Area = 26977.9
  ChamferSize = 0
  Columns = 1
  FilletRadius = 0
  Height = 226.057
  Length = 119.341
  MakeFace = true
  Placement = pos=(11.6706,10.45,-85.6886) rot=(0,0.707107,0.707107;3.14159rad)
  Rows = 1
FEATURE [Part::FeaturePython] Slice009  # WARN: FeaturePython — macro-defined, semantics opaque (R4)
  Base = -> Slice003_child002
  Mode = 1
  Tolerance = 0
  Tools = -> [Rectangle023]
FEATURE [App::DocumentObjectGroup] GrExplode_Slice009  label="Exploded Slice009"
FEATURE [Part::FeaturePython] Slice009_child0  label="Slice009.0"  # WARN: FeaturePython — macro-defined, semantics opaque (R4)
  Base = -> Slice009
  FilterType = 1
  Invert = false
  OverrideMaxVal = 0
  Placement = pos=(39,36.1,-25.5) rot=(0,0,1;0rad)
  WindowFrom = 80
  WindowTo = 100
  items = 0
FEATURE [Part::Feature] Face022
  Placement = pos=(39,36.1,-25.5) rot=(0,0,1;0rad)
  shape: bbox 38.73 x 25.55 x 0.000134 mm, 1 faces, 0 solids (baked)
FEATURE [Part::Extrusion] Extrusion040
  Base = -> Face022
  Dir = (-2.65294e-08,8.11037e-09,8.5)
  DirMode = 0
  FaceMakerClass = Part::FaceMakerBullseye
  LengthFwd = 0
  LengthRev = 0
  Solid = true
  Symmetric = false
FEATURE [Part::Feature] Face023
  Placement = pos=(162.12,-96.4028,188.001) rot=(0,0,1;3.14159rad)
  shape: bbox 5.5 x 7.1 x 0.0001336 mm, 1 faces, 0 solids (baked)
FEATURE [Part::Extrusion] Extrusion041
  Base = -> Face023
  Dir = (3.46162e-08,-5.60141e-10,8.5)
  DirMode = 0
  FaceMakerClass = Part::FaceMakerBullseye
  LengthFwd = 0
  LengthRev = 0
  Solid = true
  Symmetric = false
FEATURE [Part::MultiFuse] Fusion005002002014004003003002009002010004002003006003008008004007002004008002005011019002002002012009
  Shapes = -> [Extrusion041,Cut009,Slice009_child0,Extrusion040]
FEATURE [Part::Fuse] Fusion005002002014004003003002009002010004002003006003008008004007002004008002005011019002002002012010
  Base = -> Slice008_child1
  Tool = -> Cut011
FEATURE [Part::Fuse] Fusion005002002014004003003002009002010004002003006003008008004007002004008002005011019002002002012011
  Base = -> Slice008_child1
  Tool = -> Cut011
FEATURE [Part::Fuse] Fusion005002002014004003003002009002010004002003006003008008004007002004008002005011019002002002012013
  Base = -> Fusion005002002014004003003002009002010004002003006003008008004007002004008002005011019002002002012009
  Tool = -> Fusion005002002014004003003002009002010004002003006003008008004007002004008002005011019002002002012010
FEATURE [Part::Fuse] Fusion005002002014004003003002009002010004002003006003008008004007002004008002005011019002002002012014
  Base = -> Fusion005002002014004003003002009002010004002003006003008008004007002004008002005011019002002002012008
  Tool = -> Fusion005002002014004003003002009002010004002003006003008008004007002004008002005011019002002002012013
FEATURE [Part::Fuse] Fusion005002002014004003003002009002010004002003006003008008004007002004008002005011019002002002012015
  Base = -> Fusion005002002014004003003002009002010004002003006003008008004007002004008002005011019002002002012009
  Tool = -> Fusion005002002014004003003002009002010004002003006003008008004007002004008002005011019002002002012014
FEATURE [Part::Part2DObjectPython] Rectangle024  # Draft 2D object (typed FeaturePython)
  Area = 425.25
  ChamferSize = 0
  Columns = 1
  FilletRadius = 0
  Height = 27
  Length = 15.75
  MakeFace = true
  Placement = pos=(14,41,1.83988) rot=(0,0,1;1.5708rad)
  Rows = 1
FEATURE [Part::Extrusion] Extrusion042
  Base = -> Rectangle024
  Dir = (-8.43167e-07,-1.86136e-07,-165.413)
  DirMode = 0
  FaceMakerClass = Part::FaceMakerBullseye
  LengthFwd = 0
  LengthRev = 0
  Solid = true
  Symmetric = false
FEATURE [Part::Feature] Fusion005002002014004003003002009002010004002003006003008008004007002004008002005011019002002002012016_solid  label="Fusion005002002014004003003002009002010004002003006003008008004007002004008002005011019002002002012016 (Solid)"
  shape: bbox 151 x 112.8 x 26 mm, 233 faces (baked)
FEATURE [Part::Cut] Cut014  label="Cut015"
  Base = -> Fusion005002002014004003003002009002010004002003006003008008004007002004008002005011019002002002012015
  Tool = -> Extrusion042
FEATURE [Part::Refine] Slice004_child002  label="Slice004.002"
  Placement = pos=(162.12,-96.4028,188.001) rot=(0,0,1;3.14159rad)
  Source = -> Slice004_child0
FEATURE [Part::Part2DObjectPython] Rectangle025  # Draft 2D object (typed FeaturePython)
  Area = 1835.32
  ChamferSize = 0
  Columns = 1
  FilletRadius = 0
  Height = 46.2859
  Length = 39.6518
  MakeFace = true
  Placement = pos=(23,41,22) rot=(0,0,1;1.5708rad)
  Rows = 1
FEATURE [Part::Extrusion] Extrusion043
  Base = -> Rectangle025
  Dir = (6.81364e-08,-7.65616e-08,-20.1601)
  DirMode = 0
  FaceMakerClass = Part::FaceMakerBullseye
  LengthFwd = 0
  LengthRev = 0
  Solid = true
  Symmetric = false
FEATURE [Part::Cut] Cut015  label="Cut016"
  Base = -> Fusion005002002014004003003002009002010004002003006003008008004007002004008002005011019002002002012016_solid
  Tool = -> Extrusion043
FEATURE [Part::MultiFuse] Fusion005002002014004003003002009002010004002003006003008008004007002004008002005011019002002002012016
  Shapes = -> [Slice004_child002,Cut015]
FEATURE [Part::Refine] Fusion005002002014004003003002009002010004002003006003008008004007002004008002005011019002002002012017
  Source = -> Fusion005002002014004003003002009002010004002003006003008008004007002004008002005011019002002002012016
FEATURE [Part::Feature] Face024
  shape: bbox 22.05 x 30.6 x 0.0005974 mm, 1 faces, 0 solids (baked)
FEATURE [Part::Extrusion] Extrusion044
  Base = -> Face024
  Dir = (-1.91491e-08,6.11149e-08,8.5)
  DirMode = 0
  FaceMakerClass = Part::FaceMakerBullseye
  LengthFwd = 0
  LengthRev = 0
  Solid = true
  Symmetric = false
FEATURE [Part::Feature] Face025
  shape: bbox 37.73 x 5.001 x 0.0005979 mm, 1 faces, 0 solids (baked)
FEATURE [Part::Extrusion] Extrusion045
  Base = -> Face025
  Dir = (-2.8728e-08,3.22803e-08,8.5)
  DirMode = 0
  FaceMakerClass = Part::FaceMakerBullseye
  LengthFwd = 0
  LengthRev = 0
  Solid = true
  Symmetric = false
FEATURE [Part::Feature] Face027
  shape: bbox 38.73 x 3.501 x 0.000598 mm, 1 faces, 0 solids (baked)
FEATURE [Part::Extrusion] Extrusion046
  Base = -> Face027
  Dir = (3.48854e-09,-3.77687e-09,-0.5)
  DirMode = 0
  FaceMakerClass = Part::FaceMakerBullseye
  LengthFwd = 0
  LengthRev = 0
  Solid = true
  Symmetric = false
FEATURE [Part::MultiFuse] Fusion005002002014004003003002009002010004002003006003008008004007002004008002005011019002002002012018
  Shapes = -> [Extrusion044,Extrusion046]
FEATURE [Part::MultiFuse] Fusion005002002014004003003002009002010004002003006003008008004007002004008002005011019002002002012019
  Shapes = -> [Extrusion045,Fusion005002002014004003003002009002010004002003006003008008004007002004008002005011019002002002012018]
FEATURE [Part::MultiFuse] Fusion005002002014004003003002009002010004002003006003008008004007002004008002005011019002002002012020
  Shapes = -> [Fusion005002002014004003003002009002010004002003006003008008004007002004008002005011019002002002012017,Fusion005002002014004003003002009002010004002003006003008008004007002004008002005011019002002002012019]
FEATURE [Part::Part2DObjectPython] Rectangle026  # Draft 2D object (typed FeaturePython)
  Area = 91
  ChamferSize = 0
  Columns = 1
  FilletRadius = 0
  Height = 26
  Length = 3.5
  MakeFace = true
  Placement = pos=(24,68.6,-4) rot=(0.57735,0.57735,0.57735;2.0944rad)
  Rows = 1
FEATURE [Part::Extrusion] Extrusion047
  Base = -> Rectangle026
  Dir = (112,-1.11652e-09,3.49563e-07)
  DirMode = 0
  FaceMakerClass = Part::FaceMakerBullseye
  LengthFwd = 0
  LengthRev = 0
  Solid = true
  Symmetric = false
FEATURE [Part::MultiFuse] Fusion005002002014004003003002009002010004002003006003008008004007002004008002005011019002002002012021
  Shapes = -> [Fusion005002002014004003003002009002010004002003006003008008004007002004008002005011019002002002012020,Extrusion047]
FEATURE [Part::Feature] Face028
  shape: bbox 0.0005977 x 1.501 x 5.84 mm, 1 faces, 0 solids (baked)
FEATURE [Part::Extrusion] Extrusion048
  Base = -> Face028
  Dir = (0.27,-1e-16,4.3513e-12)
  DirMode = 0
  FaceMakerClass = Part::FaceMakerBullseye
  LengthFwd = 0
  LengthRev = 0
  Solid = true
  Symmetric = false
FEATURE [Part::Cut] Cut016  label="Cut017"
  Base = -> Fusion005002002014004003003002009002010004002003006003008008004007002004008002005011019002002002012021
  Tool = -> Extrusion048
FEATURE [Part::Feature] Face029
  shape: bbox 0.0005972 x 29.1 x 8.501 mm, 1 faces, 0 solids (baked)
FEATURE [Part::Extrusion] Extrusion049
  Base = -> Face029
  Dir = (-0.27,2.17842e-11,-6.08264e-10)
  DirMode = 0
  FaceMakerClass = Part::FaceMakerBullseye
  LengthFwd = 0
  LengthRev = 0
  Solid = true
  Symmetric = false
FEATURE [Part::Feature] Face030
  shape: bbox 0.0005977 x 2.001 x 8.501 mm, 1 faces, 0 solids (baked)
FEATURE [Part::Extrusion] Extrusion050
  Base = -> Face030
  Dir = (-0.27,1.96086e-11,-9.12536e-10)
  DirMode = 0
  FaceMakerClass = Part::FaceMakerBullseye
  LengthFwd = 0
  LengthRev = 0
  Solid = true
  Symmetric = false
FEATURE [Part::Feature] Face031
  shape: bbox 0.0005979 x 31.1 x 17 mm, 1 faces, 0 solids (baked)
FEATURE [Part::Extrusion] Extrusion051
  Base = -> Face031
  Dir = (-0.27,1.69301e-11,-1.83619e-09)
  DirMode = 0
  FaceMakerClass = Part::FaceMakerBullseye
  LengthFwd = 0
  LengthRev = 0
  Solid = true
  Symmetric = false
FEATURE [Part::Feature] Face032
  shape: bbox 0.0005978 x 1.501 x 5.84 mm, 1 faces, 0 solids (baked)
FEATURE [Part::Extrusion] Extrusion052
  Base = -> Face032
  Dir = (-0.27,1e-16,-4.3513e-12)
  DirMode = 0
  FaceMakerClass = Part::FaceMakerBullseye
  LengthFwd = 0
  LengthRev = 0
  Solid = true
  Symmetric = false
FEATURE [Part::MultiFuse] Fusion005002002014004003003002009002010004002003006003008008004007002004008002005011019002002002012022
  Shapes = -> [Extrusion052,Extrusion051,Extrusion050,Extrusion049,Cut016]
FEATURE [Part::Refine] Fusion005002002014004003003002009002010004002003006003008008004007002004008002005011019002002002012023
  Source = -> Fusion005002002014004003003002009002010004002003006003008008004007002004008002005011019002002002012022
FEATURE [Part::Part2DObjectPython] Rectangle027  # Draft 2D object (typed FeaturePython)
  Area = 174.839
  ChamferSize = 0
  Columns = 1
  FilletRadius = 0
  Height = 35.4803
  Length = 4.92778
  MakeFace = true
  Placement = pos=(23,63.1,-1.5) rot=(0.57735,0.57735,0.57735;2.0944rad)
  Rows = 1
FEATURE [Part::Extrusion] Extrusion053
  Base = -> Rectangle027
  Dir = (39.3726,3.63723e-08,1.52529e-08)
  DirMode = 0
  FaceMakerClass = Part::FaceMakerBullseye
  LengthFwd = 0
  LengthRev = 0
  Solid = true
  Symmetric = false
FEATURE [Part::Cut] Cut017  label="Cut018"
  Base = -> Fusion005002002014004003003002009002010004002003006003008008004007002004008002005011019002002002012023
  Tool = -> Extrusion053
FEATURE [Part::Part2DObjectPython] Rectangle028  # Draft 2D object (typed FeaturePython)
  Area = 152.75
  ChamferSize = 0
  Columns = 1
  FilletRadius = 0
  Height = 11.75
  Length = 13
  MakeFace = true
  Placement = pos=(-13,39.5,10.25) rot=(1,0,0;1.5708rad)
  Rows = 1
FEATURE [Part::Extrusion] Extrusion054
  Base = -> Rectangle028
  Dir = (5.93727e-09,7.05,-3.33513e-08)
  DirMode = 0
  FaceMakerClass = Part::FaceMakerBullseye
  LengthFwd = 0
  LengthRev = 0
  Solid = true
  Symmetric = false
FEATURE [Part::Cut] Cut018  label="Cut019"
  Base = -> Cut017
  Tool = -> Extrusion054
FEATURE [Part::Feature] Face033
  shape: bbox 90 x 0.0005982 x 2.501 mm, 1 faces, 0 solids (baked)
FEATURE [Part::Extrusion] Extrusion055
  Base = -> Face033
  Dir = (2e-16,-0.5,1.96003e-11)
  DirMode = 0
  FaceMakerClass = Part::FaceMakerBullseye
  LengthFwd = 0
  LengthRev = 0
  Solid = true
  Symmetric = false
FEATURE [Part::MultiFuse] Fusion005002002014004003003002009002010004002003006003008008004007002004008002005011019002002002012024
  Shapes = -> [Extrusion055,Cut018]
FEATURE [Part::Part2DObjectPython] Line032  # Draft 2D object (typed FeaturePython)
  Area = 0
  ChamferSize = 0
  Closed = false
  End = (136,68.6,-1.5)
  FilletRadius = 0
  Length = 15
  MakeFace = true
  Placement = pos=(136,68.6,13.5) rot=(0.57735,0.57735,0.57735;2.0944rad)
  Points = (2) [(0,0,0),(0,-15,-1.01897e-08)]
  Start = (136,68.6,13.5)
  Subdivisions = 0
FEATURE [Part::Part2DObjectPython] Rectangle029  # Draft 2D object (typed FeaturePython)
  Area = 3286.04
  ChamferSize = 0
  Columns = 1
  FilletRadius = 0
  Height = 92.1995
  Length = 35.6405
  MakeFace = true
  Placement = pos=(162.699,32.9595,-1.5) rot=(0,0,1;1.5708rad)
  Rows = 1
FEATURE [Part::FeaturePython] Slice010  # WARN: FeaturePython — macro-defined, semantics opaque (R4)
  Base = -> Fusion005002002014004003003002009002010004002003006003008008004007002004008002005011019002002002012024
  Mode = 1
  Tolerance = 0
  Tools = -> [Rectangle029]
FEATURE [Part::FeaturePython] Slice010_child0  label="Slice010.0"  # WARN: FeaturePython — macro-defined, semantics opaque (R4)
  Base = -> Slice010
  FilterType = 1
  Invert = false
  OverrideMaxVal = 0
  WindowFrom = 80
  WindowTo = 100
  items = 0
FEATURE [App::DocumentObjectGroup] GrExplode_Slice010  label="Exploded Slice010"
  Group = -> [Slice010_child0]
FEATURE [Part::FeaturePython] Slice010_child1  label="Slice010.1"  # WARN: FeaturePython — macro-defined, semantics opaque (R4)
  Base = -> Slice010
  FilterType = 1
  Invert = false
  OverrideMaxVal = 0
  WindowFrom = 80
  WindowTo = 100
  items = 1
FEATURE [Part::Part2DObjectPython] Rectangle030  # Draft 2D object (typed FeaturePython)
  Area = 4402.41
  ChamferSize = 0
  Columns = 1
  FilletRadius = 0
  Height = 49.9579
  Length = 88.1224
  MakeFace = true
  Placement = pos=(74.5761,68.6,-1.5) rot=(1,0,0;1.5708rad)
  Rows = 1
FEATURE [Part::FeaturePython] Slice011  # WARN: FeaturePython — macro-defined, semantics opaque (R4)
  Base = -> Slice010_child0
  Mode = 1
  Tolerance = 0
  Tools = -> [Rectangle030]
FEATURE [Part::FeaturePython] Slice011_child0  label="Slice011.0"  # WARN: FeaturePython — macro-defined, semantics opaque (R4)
  Base = -> Slice011
  FilterType = 1
  Invert = false
  OverrideMaxVal = 0
  WindowFrom = 80
  WindowTo = 100
  items = 0
FEATURE [Part::FeaturePython] Slice011_child1  label="Slice011.1"  # WARN: FeaturePython — macro-defined, semantics opaque (R4)
  Base = -> Slice011
  FilterType = 1
  Invert = false
  OverrideMaxVal = 0
  WindowFrom = 80
  WindowTo = 100
  items = 1
FEATURE [Part::MultiFuse] Fusion005002002014004003003002009002010004002003006003008008004007002004008002005011019002002002012025
  Placement = pos=(-1.137e-13,1.5,-1.0552e-09) rot=(0,0,1;0rad)
  Shapes = -> [Slice010_child1,Slice011_child1]
FEATURE [Part::Feature] Face034
  Placement = pos=(-1.137e-13,1.5,-1.0552e-09) rot=(0,0,1;0rad)
  shape: bbox 7.001 x 0.0005982 x 13.5 mm, 1 faces, 0 solids (baked)
FEATURE [Part::Extrusion] Extrusion056
  Base = -> Face034
  Dir = (1.99e-14,-1.5,1.92988e-10)
  DirMode = 0
  FaceMakerClass = Part::FaceMakerBullseye
  LengthFwd = 0
  LengthRev = 0
  Solid = true
  Symmetric = false
FEATURE [Part::MultiFuse] Fusion005002002014004003003002009002010004002003006003008008004007002004008002005011019002002002012026
  Shapes = -> [Fusion005002002014004003003002009002010004002003006003008008004007002004008002005011019002002002012025,Extrusion056]
FEATURE [Part::Part2DObjectPython] Rectangle031  # Draft 2D object (typed FeaturePython)
  Area = 67.8058
  ChamferSize = 0
  Columns = 1
  FilletRadius = 0
  Height = 5.6
  Length = 12.1082
  MakeFace = true
  Placement = pos=(90.8918,68.6,1.9) rot=(1,0,0;1.5708rad)
  Rows = 1
FEATURE [Part::Extrusion] Extrusion057
  Base = -> Rectangle031
  Dir = (1.74457e-11,1.75,-3.25244e-09)
  DirMode = 0
  FaceMakerClass = Part::FaceMakerBullseye
  LengthFwd = 0
  LengthRev = 0
  Solid = true
  Symmetric = false
FEATURE [Part::Cut] Cut019  label="Cut020"
  Base = -> Slice011_child0
  Tool = -> Extrusion057
FEATURE [Part::Feature] Face035
  Placement = pos=(81.7528,194.877,-8.54915) rot=(0,0,-1;1.5708rad)
  shape: bbox 17.5 x 33 x 0.0005987 mm, 1 faces, 0 solids (baked)
FEATURE [Part::Extrusion] Extrusion058
  Base = -> Face035
  Dir = (-2.35168e-10,2.22287e-10,-2.5)
  DirMode = 0
  FaceMakerClass = Part::FaceMakerBullseye
  LengthFwd = 0
  LengthRev = 0
  Solid = true
  Symmetric = false
FEATURE [Part::Part2DObjectPython] Line034  # Draft 2D object (typed FeaturePython)
  Area = 0
  ChamferSize = 0
  Closed = false
  End = (136,-37,-1.5)
  FilletRadius = 0
  Length = 13
  MakeFace = true
  Placement = pos=(136,-24,-1.5) rot=(0,0,1;1.5708rad)
  Points = (2) [(0,0,0),(-13,0,8.86251e-09)]
  Start = (136,-24,-1.5)
  Subdivisions = 0
FEATURE [Part::Part2DObjectPython] Rectangle032  # Draft 2D object (typed FeaturePython)
  Area = 3356.07
  ChamferSize = 0
  Columns = 1
  FilletRadius = 0
  Height = 30.7614
  Length = 109.1
  MakeFace = true
  Placement = pos=(166.761,-37,-1.5) rot=(0,0,1;1.5708rad)
  Rows = 1
FEATURE [Part::Extrusion] Extrusion059
  Base = -> Rectangle032
  Dir = (-1.1501e-09,1.70433e-09,-2.5)
  DirMode = 0
  FaceMakerClass = Part::FaceMakerBullseye
  LengthFwd = 0
  LengthRev = 0
  Solid = true
  Symmetric = false
FEATURE [Part::MultiFuse] Fusion005002002014004003003002009002010004002003006003008008004007002004008002005011019002002002012027
  Shapes = -> [Cut019,Fusion005002002014004003003002009002010004002003006003008008004007002004008002005011019002002002012026]
FEATURE [Part::MultiFuse] Fusion005002002014004003003002009002010004002003006003008008004007002004008002005011019002002002012028
  Shapes = -> [Fusion005002002014004003003002009002010004002003006003008008004007002004008002005011019002002002012027,Extrusion059]
FEATURE [Part::Refine] Slice_child002  label="Slice.002"
  Placement = pos=(-8.08898,-10.5972,188.001) rot=(0,0,1;0rad)
  Source = -> Slice_child0
FEATURE [Part::MultiFuse] Fusion005002002014004003003002009002010004002003006003008008004007002004008002005011019002002002012029
  Placement = pos=(-2,1.03034e-09,-1.74283e-08) rot=(0,0,1;0rad)
  Shapes = -> [Slice_child002,Slice_child0]
FEATURE [Part::Feature] Face036
  Placement = pos=(202.064,130.95,188.001) rot=(0,0,-1;1.5708rad)
  shape: bbox 2 x 97.4 x 0.0001336 mm, 1 faces, 0 solids (baked)
FEATURE [Part::Extrusion] Extrusion060
  Base = -> Face036
  Dir = (-4.2347e-09,-1.60786e-09,-21.5)
  DirMode = 0
  FaceMakerClass = Part::FaceMakerBullseye
  LengthFwd = 0
  LengthRev = 0
  Solid = true
  Symmetric = false
FEATURE [Part::Cut] Cut020  label="Cut021"
  Base = -> Fusion005002002014004003003002009002010004002003006003008008004007002004008002005011019002002002012029
  Tool = -> Extrusion060
FEATURE [Part::Feature] Face037
  shape: bbox 2 x 0.0001336 x 23.5 mm, 1 faces, 0 solids (baked)
FEATURE [Part::Extrusion] Extrusion061
  Base = -> Face037
  Dir = (2.0535e-10,20.6,-3.53035e-09)
  DirMode = 0
  FaceMakerClass = Part::FaceMakerBullseye
  LengthFwd = 0
  LengthRev = 0
  Solid = true
  Symmetric = false
FEATURE [Part::Feature] Face038
  shape: bbox 0.0005983 x 1.501 x 15 mm, 1 faces, 0 solids (baked)
FEATURE [Part::Extrusion] Extrusion062
  Base = -> Face038
  Dir = (28.7614,1.72389e-09,1.51627e-08)
  DirMode = 0
  FaceMakerClass = Part::FaceMakerBullseye
  LengthFwd = 0
  LengthRev = 0
  Solid = true
  Symmetric = false
FEATURE [Part::Feature] Face039
  shape: bbox 0.0005983 x 3.501 x 23.5 mm, 1 faces, 0 solids (baked)
FEATURE [Part::Extrusion] Extrusion063
  Base = -> Face039
  Dir = (30.7614,1.84376e-09,1.62171e-08)
  DirMode = 0
  FaceMakerClass = Part::FaceMakerBullseye
  LengthFwd = 0
  LengthRev = 0
  Solid = true
  Symmetric = false
FEATURE [Part::MultiFuse] Fusion005002002014004003003002009002010004002003006003008008004007002004008002005011019002002002012030
  Shapes = -> [Extrusion062,Extrusion063,Cut020,Extrusion061]
FEATURE [Part::Feature] Face040
  shape: bbox 2 x 0.0001336 x 23.5 mm, 1 faces, 0 solids (baked)
FEATURE [Part::Extrusion] Extrusion064
  Base = -> Face040
  Dir = (-3.84704e-11,8.9,-2.22768e-09)
  DirMode = 0
  FaceMakerClass = Part::FaceMakerBullseye
  LengthFwd = 0
  LengthRev = 0
  Solid = true
  Symmetric = false
FEATURE [Part::Cut] Cut021  label="Cut022"
  Base = -> Fusion005002002014004003003002009002010004002003006003008008004007002004008002005011019002002002012030
  Tool = -> Extrusion064
FEATURE [Part::MultiFuse] Fusion005002002014004003003002009002010004002003006003008008004007002004008002005011019002002002012031
  Shapes = -> [Cut021,Fusion005002002014004003003002009002010004002003006003008008004007002004008002005011019002002002012028]
FEATURE [App::DocumentObjectGroup] GrExplode_Slice011  label="Exploded Slice011"
  Group = -> [Fusion005002002014004003003002009002010004002003006003008008004007002004008002005011019002002002012031]
FEATURE [Part::Refine] Fusion005002002014004003003002009002010004002003006003008008004007002004008002005011019002002002012032
  Source = -> Fusion005002002014004003003002009002010004002003006003008008004007002004008002005011019002002002012031
FEATURE [Part::Part2DObjectPython] Line  # Draft 2D object (typed FeaturePython)
  Area = 0
  ChamferSize = 0
  Closed = false
  End = (136,-33.5,22)
  FilletRadius = 0
  Length = 3.5
  MakeFace = true
  Placement = pos=(136,-37,22) rot=(0.57735,0.57735,0.57735;2.0944rad)
  Points = (2) [(0,0,0),(3.5,0,0)]
  Start = (136,-37,22)
  Subdivisions = 0
FEATURE [Part::Part2DObjectPython] Rectangle033  # Draft 2D object (typed FeaturePython)
  Area = 82.25
  ChamferSize = 0
  Columns = 1
  FilletRadius = 0
  Height = 23.5
  Length = 3.5
  MakeFace = true
  Placement = pos=(136,-37,-1.5) rot=(0.57735,0.57735,0.57735;2.0944rad)
  Rows = 1
FEATURE [Part::Extrusion] Extrusion065
  Base = -> Rectangle033
  Dir = (28.7614,1.72388e-09,1.51627e-08)
  DirMode = 0
  FaceMakerClass = Part::FaceMakerBullseye
  LengthFwd = 0
  LengthRev = 0
  Solid = true
  Symmetric = false
FEATURE [Part::Part2DObjectPython] Circle005  # Draft 2D object (typed FeaturePython)
  Area = 28.2743
  FirstAngle = 0
  LastAngle = 0
  MakeFace = true
  Placement = pos=(147.261,31.5,6.5) rot=(0.57735,-0.57735,-0.57735;2.0944rad)
  Radius = 3
FEATURE [Part::Part2DObjectPython] Circle006  # Draft 2D object (typed FeaturePython)
  Area = 28.2743
  FirstAngle = 0
  LastAngle = 0
  MakeFace = true
  Placement = pos=(147.261,16.5,6.5) rot=(0.57735,-0.57735,-0.57735;2.0944rad)
  Radius = 3
FEATURE [Part::Extrusion] Extrusion066
  Base = -> Circle006
  Dir = (3.72676,-2.65e-14,-1.94767e-10)
  DirMode = 0
  FaceMakerClass = Part::FaceMakerBullseye
  LengthFwd = 0
  LengthRev = 0
  Solid = true
  Symmetric = false
FEATURE [Part::Extrusion] Extrusion067
  Base = -> Circle005
  Dir = (3.72676,-2.65e-14,-1.94767e-10)
  DirMode = 0
  FaceMakerClass = Part::FaceMakerBullseye
  LengthFwd = 0
  LengthRev = 0
  Solid = true
  Symmetric = false
FEATURE [Part::Part2DObjectPython] Rectangle034  # Draft 2D object (typed FeaturePython)
  Area = 90
  ChamferSize = 0
  Columns = 1
  FilletRadius = 0
  Height = 6
  Length = 15
  MakeFace = true
  Placement = pos=(147.261,31.5,3.5) rot=(0.57735,-0.57735,-0.57735;2.0944rad)
  Rows = 1
FEATURE [Part::Extrusion] Extrusion068
  Base = -> Rectangle034
  Dir = (3.72676,-2.65e-14,-1.94767e-10)
  DirMode = 0
  FaceMakerClass = Part::FaceMakerBullseye
  LengthFwd = 0
  LengthRev = 0
  Solid = true
  Symmetric = false
FEATURE [Part::Cut] Cut022  label="Cut023"
  Base = -> Fusion005002002014004003003002009002010004002003006003008008004007002004008002005011019002002002012032
  Tool = -> Extrusion068
FEATURE [Part::Cut] Cut023  label="Cut024"
  Base = -> Cut022
  Tool = -> Extrusion066
FEATURE [Part::Cut] Cut024  label="Cut025"
  Base = -> Cut023
  Tool = -> Extrusion067
FEATURE [Part::MultiFuse] Fusion005002002014004003003002009002010004002003006003008008004007002004008002005011019002002002012033
  Shapes = -> [Cut024,Extrusion065]
